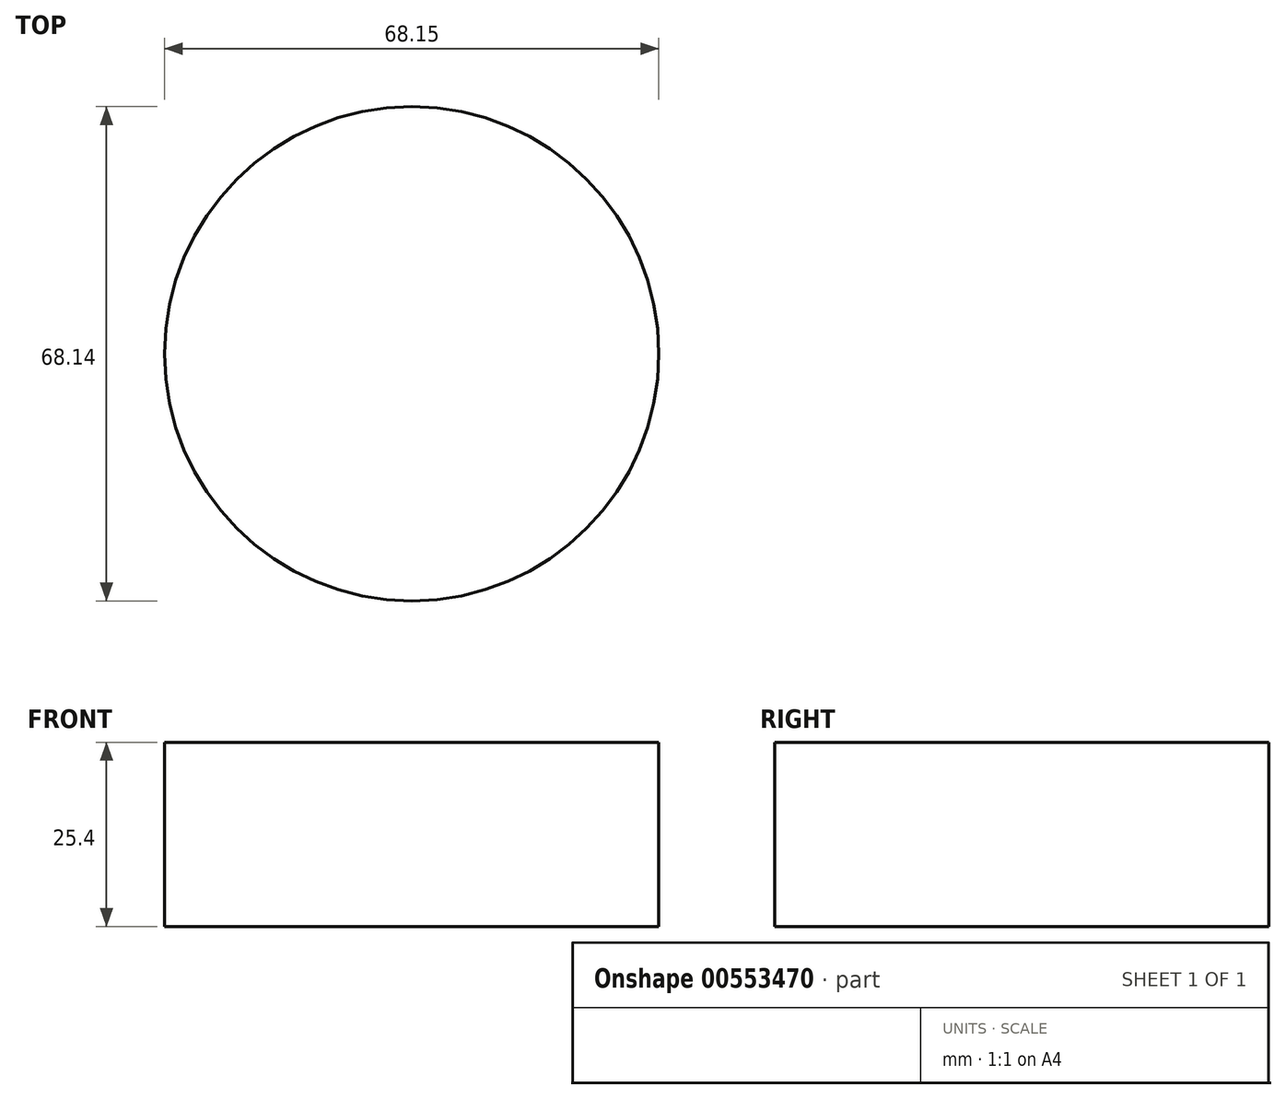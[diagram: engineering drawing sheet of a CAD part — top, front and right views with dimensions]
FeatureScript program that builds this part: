
annotation { "Feature Type Name" : "Feature", "Feature Type Description" : "" }
export const myFeature = defineFeature(function(context is Context, id is Id, definition is map)
    precondition{}
    {
        {
            var Q0;
            Q0=qCreatedBy(makeId("Top.planeOp"),FACE);
            var sketch = newSketch(context, id + "F0", { "sketchPlane" : qUnion([Q0])});
            skCircle(sketch, "E0", {"center": v(-53.21, 23.28) * mm, "radius": 34.07 * mm});
            skSolve(sketch);
        }
        {
            var Q0;
            Q0=makeQuery(id+"F0.imprint","IMPRINT",FACE,{"disambiguationData":[TD([[makeQuery(id+"F0.imprint","IMPRINT",EDGE,{"derivedFrom":sQuery(id+"F0.wireOp",EDGE,"E0")}),1.0]])]});
            extrude(context, id + "F1", {"entities" : qUnion([Q0]), "endBound" : BoundingType.SYMMETRIC, "depth" : 25.4 * mm, "offsetDistance" : 25.4 * mm});
        }
    });
